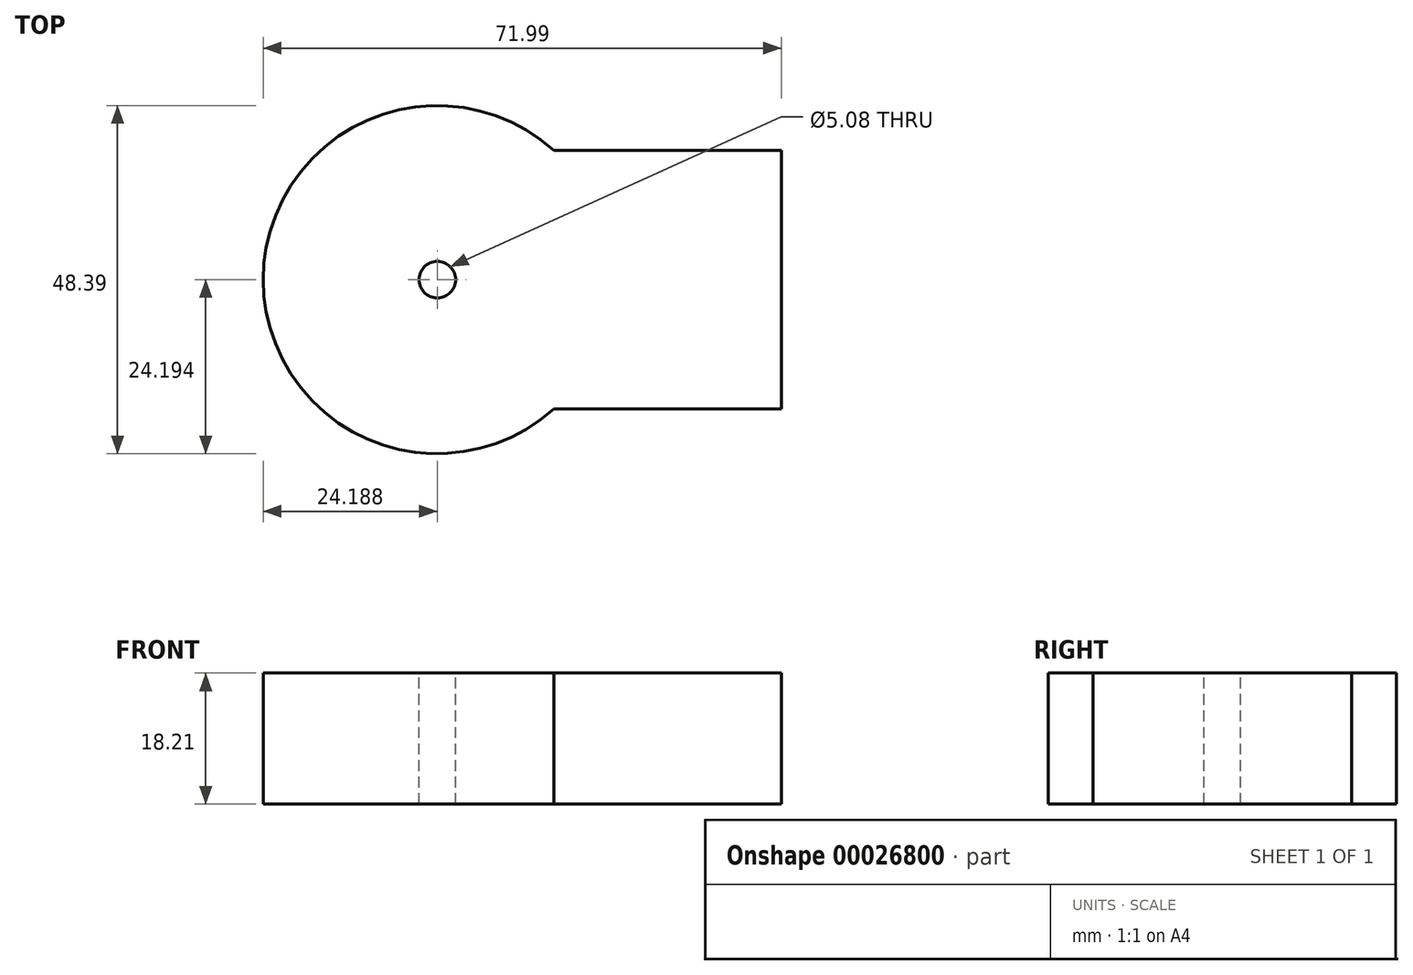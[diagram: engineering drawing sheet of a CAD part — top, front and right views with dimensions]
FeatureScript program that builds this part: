
annotation { "Feature Type Name" : "Feature", "Feature Type Description" : "" }
export const myFeature = defineFeature(function(context is Context, id is Id, definition is map)
    precondition{}
    {
        {
            var Q0;
            Q0=qCreatedBy(makeId("Top.planeOp"),FACE);
            var sketch = newSketch(context, id + "F0", { "sketchPlane" : qUnion([Q0])});
            skArc(sketch, "E0", {"start": v(-6.44, 28.7) * mm, "mid": v(-46.83, 10.74) * mm, "end": v(-6.44, -7.22) * mm});
            skLineSegment(sketch, "E1", {"start": v(-6.44, 28.7) * mm, "end": v(-6.44, -7.22) * mm});
            skSolve(sketch);
        }
        {
            var Q0;
            Q0=makeQuery(id+"F0.imprint","IMPRINT",FACE,{"disambiguationData":[TD([[makeQuery(id+"F0.imprint","IMPRINT",EDGE,{"derivedFrom":sQuery(id+"F0.wireOp",EDGE,"E0")}),1.0]])]});
            extrude(context, id + "F1", {"entities" : qUnion([Q0]), "depth" : 18.2 * mm});
        }
        {
            var Q0;
            Q0=makeQuery(id+"F1.opExtrude","CAP_FACE",FACE,{"disambiguationData":[OSD([sQuery(id+"F0.wireOp",EDGE,"E0"),sQuery(id+"F0.wireOp",EDGE,"E1")])],"isStart":false});
            var sketch = newSketch(context, id + "F2", { "sketchPlane" : qUnion([Q0])});
            skCircle(sketch, "E2", {"center": v(-22.64, 10.74) * mm, "radius": 2.54 * mm});
            skSolve(sketch);
        }
        {
            var Q0;
            Q0=makeQuery(id+"F2.imprint","IMPRINT",FACE,{"disambiguationData":[TD([[makeQuery(id+"F2.imprint","IMPRINT",EDGE,{"derivedFrom":sQuery(id+"F2.wireOp",EDGE,"E2")}),1.0]])]});
            extrude(context, id + "F3", {"entities" : qUnion([Q0]), "operationType" : NewBodyOperationType.REMOVE, "oppositeDirection" : true, "depth" : 25.4 * mm});
        }
        {
            var Q0;
            Q0=makeQuery(id+"F1.opExtrude","SWEPT_FACE",FACE,{"disambiguationData":[OSD([sQuery(id+"F0.wireOp",EDGE,"E1")])]});
            extrude(context, id + "F4", {"entities" : qUnion([Q0]), "operationType" : NewBodyOperationType.ADD, "depth" : 31.6 * mm});
        }
    });
